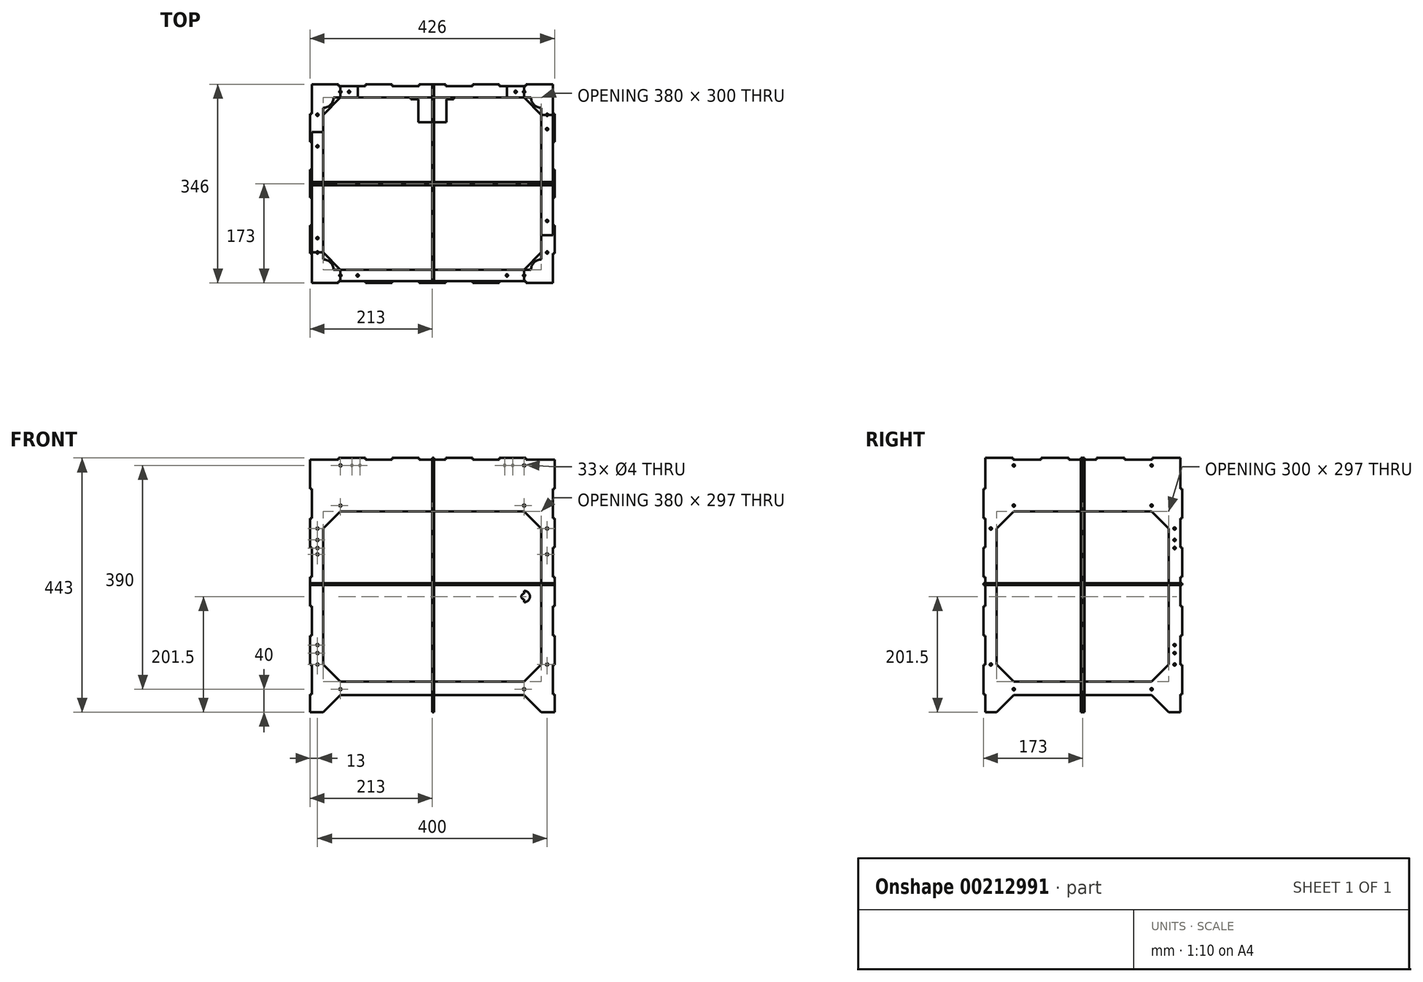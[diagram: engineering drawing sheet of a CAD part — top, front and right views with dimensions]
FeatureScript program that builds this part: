
annotation { "Feature Type Name" : "Feature", "Feature Type Description" : "" }
export const myFeature = defineFeature(function(context is Context, id is Id, definition is map)
    precondition{}
    {
        {
            assignVariable(context, id + "F0", {"name" : "thick", "anyValue" : 3});
        }
        {
            var Q0;
            Q0=qCreatedBy(makeId("Top.planeOp"),FACE);
            var sketch = newSketch(context, id + "F1", { "sketchPlane" : qUnion([Q0])});
            skLineSegment(sketch, "E0.bottom", {"start": v(213, -173) * mm, "end": v(-213, -173) * mm});
            skLineSegment(sketch, "E0.top", {"start": v(213, 173) * mm, "end": v(-213, 173) * mm});
            skLineSegment(sketch, "E0.left", {"start": v(213, -173) * mm, "end": v(213, 173) * mm});
            skLineSegment(sketch, "E0.right", {"start": v(-213, -173) * mm, "end": v(-213, 173) * mm});
            skPoint(sketch, "E0.middle", {"position": v(0, 0) * mm});
            skLineSegment(sketch, "E1.bottom", {"start": v(160, -150) * mm, "end": v(-160, -150) * mm});
            skLineSegment(sketch, "E1.top", {"start": v(160, 150) * mm, "end": v(-160, 150) * mm});
            skLineSegment(sketch, "E1.left", {"start": v(190, -120) * mm, "end": v(190, 120) * mm});
            skLineSegment(sketch, "E1.right", {"start": v(-190, -120) * mm, "end": v(-190, 120) * mm});
            skLineSegment(sketch, "E2", {"start": v(-160, 150) * mm, "end": v(-190, 120) * mm});
            skLineSegment(sketch, "E3", {"start": v(-190, -120) * mm, "end": v(-160, -150) * mm});
            skLineSegment(sketch, "E4", {"start": v(190, -120) * mm, "end": v(160, -150) * mm});
            skLineSegment(sketch, "E5", {"start": v(190, 120) * mm, "end": v(160, 150) * mm});
            skPoint(sketch, "E6.orphan", {"position": v(-190, 150) * mm});
            skPoint(sketch, "E7.orphan", {"position": v(-190, -150) * mm});
            skPoint(sketch, "E8.orphan", {"position": v(190, -150) * mm});
            skPoint(sketch, "E9.orphan", {"position": v(190, 150) * mm});
            skCircle(sketch, "E10", {"center": v(-160, 160) * mm, "radius": 2 * mm});
            skCircle(sketch, "E11", {"center": v(160, 160) * mm, "radius": 2 * mm});
            skCircle(sketch, "E12", {"center": v(-200, 120) * mm, "radius": 2 * mm});
            skCircle(sketch, "E13", {"center": v(-200, -120) * mm, "radius": 2 * mm});
            skCircle(sketch, "E14", {"center": v(-160, -160) * mm, "radius": 2 * mm});
            skCircle(sketch, "E15", {"center": v(160, -160) * mm, "radius": 2 * mm});
            skCircle(sketch, "E16", {"center": v(200, -120) * mm, "radius": 2 * mm});
            skCircle(sketch, "E17", {"center": v(200, 120) * mm, "radius": 2 * mm});
            skLineSegment(sketch, "E18", {"start": v(-163.33, -173) * mm, "end": v(-163.33, -170) * mm});
            skLineSegment(sketch, "E19", {"start": v(-163.33, -170) * mm, "end": v(-116.67, -170) * mm});
            skLineSegment(sketch, "E20", {"start": v(-116.67, -170) * mm, "end": v(-116.67, -173) * mm});
            skLineSegment(sketch, "E21.1.0.0", {"start": v(-70, -173) * mm, "end": v(-70, -170) * mm});
            skLineSegment(sketch, "E21.1.0.1", {"start": v(-70, -170) * mm, "end": v(-23.33, -170) * mm});
            skLineSegment(sketch, "E21.1.0.2", {"start": v(-23.33, -170) * mm, "end": v(-23.33, -173) * mm});
            skLineSegment(sketch, "E21.2.0.0", {"start": v(23.33, -173) * mm, "end": v(23.33, -170) * mm});
            skLineSegment(sketch, "E21.2.0.1", {"start": v(23.33, -170) * mm, "end": v(70, -170) * mm});
            skLineSegment(sketch, "E21.2.0.2", {"start": v(70, -170) * mm, "end": v(70, -173) * mm});
            skLineSegment(sketch, "E21.3.0.0", {"start": v(116.67, -173) * mm, "end": v(116.67, -170) * mm});
            skLineSegment(sketch, "E21.3.0.1", {"start": v(116.67, -170) * mm, "end": v(163.33, -170) * mm});
            skLineSegment(sketch, "E21.3.0.2", {"start": v(163.33, -170) * mm, "end": v(163.33, -173) * mm});
            skLineSegment(sketch, "E21.direction1", {"start": v(-163.33, -173) * mm, "end": v(-70, -173) * mm, "construction": true});
            skLineSegment(sketch, "E22", {"start": v(-163.33, 173) * mm, "end": v(-163.33, 170) * mm});
            skLineSegment(sketch, "E23", {"start": v(-163.33, 170) * mm, "end": v(-116.67, 170) * mm});
            skLineSegment(sketch, "E24", {"start": v(-116.67, 170) * mm, "end": v(-116.67, 173) * mm});
            skLineSegment(sketch, "E25.1.0.0", {"start": v(-70, 173) * mm, "end": v(-70, 170) * mm});
            skLineSegment(sketch, "E25.1.0.1", {"start": v(-70, 170) * mm, "end": v(-23.33, 170) * mm});
            skLineSegment(sketch, "E25.1.0.2", {"start": v(-23.33, 170) * mm, "end": v(-23.33, 173) * mm});
            skLineSegment(sketch, "E25.2.0.0", {"start": v(23.33, 173) * mm, "end": v(23.33, 170) * mm});
            skLineSegment(sketch, "E25.2.0.1", {"start": v(23.33, 170) * mm, "end": v(70, 170) * mm});
            skLineSegment(sketch, "E25.2.0.2", {"start": v(70, 170) * mm, "end": v(70, 173) * mm});
            skLineSegment(sketch, "E25.3.0.0", {"start": v(116.67, 173) * mm, "end": v(116.67, 170) * mm});
            skLineSegment(sketch, "E25.3.0.1", {"start": v(116.67, 170) * mm, "end": v(163.33, 170) * mm});
            skLineSegment(sketch, "E25.3.0.2", {"start": v(163.33, 170) * mm, "end": v(163.33, 173) * mm});
            skLineSegment(sketch, "E25.direction1", {"start": v(-163.33, 170) * mm, "end": v(-70, 170) * mm, "construction": true});
            skLineSegment(sketch, "E26", {"start": v(-213, -121.43) * mm, "end": v(-210, -121.43) * mm});
            skLineSegment(sketch, "E27", {"start": v(-210, -121.43) * mm, "end": v(-210, -170) * mm});
            skLineSegment(sketch, "E28", {"start": v(-210, -170) * mm, "end": v(-213, -170) * mm});
            skLineSegment(sketch, "E29.0.1.0", {"start": v(-213, -24.29) * mm, "end": v(-210, -24.29) * mm});
            skLineSegment(sketch, "E29.0.1.1", {"start": v(-210, -24.29) * mm, "end": v(-210, -72.86) * mm});
            skLineSegment(sketch, "E29.0.1.2", {"start": v(-210, -72.86) * mm, "end": v(-213, -72.86) * mm});
            skLineSegment(sketch, "E29.0.2.0", {"start": v(-213, 72.86) * mm, "end": v(-210, 72.86) * mm});
            skLineSegment(sketch, "E29.0.2.1", {"start": v(-210, 72.86) * mm, "end": v(-210, 24.29) * mm});
            skLineSegment(sketch, "E29.0.2.2", {"start": v(-210, 24.29) * mm, "end": v(-213, 24.29) * mm});
            skLineSegment(sketch, "E29.0.3.0", {"start": v(-213, 170) * mm, "end": v(-210, 170) * mm});
            skLineSegment(sketch, "E29.0.3.1", {"start": v(-210, 170) * mm, "end": v(-210, 121.43) * mm});
            skLineSegment(sketch, "E29.0.3.2", {"start": v(-210, 121.43) * mm, "end": v(-213, 121.43) * mm});
            skLineSegment(sketch, "E29.direction1", {"start": v(-213, -121.43) * mm, "end": v(-188, -121.43) * mm, "construction": true});
            skLineSegment(sketch, "E29.direction2", {"start": v(-213, -121.43) * mm, "end": v(-213, -24.29) * mm, "construction": true});
            skLineSegment(sketch, "E30", {"start": v(-210, -173) * mm, "end": v(-210, -170) * mm});
            skLineSegment(sketch, "E31", {"start": v(-210, 173) * mm, "end": v(-210, 170) * mm});
            skLineSegment(sketch, "E32", {"start": v(210, -173) * mm, "end": v(210, -170) * mm});
            skLineSegment(sketch, "E33", {"start": v(210, 173) * mm, "end": v(210, 170) * mm});
            skLineSegment(sketch, "E34", {"start": v(213, -170) * mm, "end": v(210, -170) * mm});
            skLineSegment(sketch, "E35", {"start": v(210, -170) * mm, "end": v(210, -121.43) * mm});
            skLineSegment(sketch, "E36", {"start": v(210, -121.43) * mm, "end": v(213, -121.43) * mm});
            skLineSegment(sketch, "E37.0.1.0", {"start": v(210, -24.29) * mm, "end": v(213, -24.29) * mm});
            skLineSegment(sketch, "E37.0.1.1", {"start": v(210, -72.86) * mm, "end": v(210, -24.29) * mm});
            skLineSegment(sketch, "E37.0.1.2", {"start": v(213, -72.86) * mm, "end": v(210, -72.86) * mm});
            skLineSegment(sketch, "E37.0.2.0", {"start": v(210, 72.86) * mm, "end": v(213, 72.86) * mm});
            skLineSegment(sketch, "E37.0.2.1", {"start": v(210, 24.29) * mm, "end": v(210, 72.86) * mm});
            skLineSegment(sketch, "E37.0.2.2", {"start": v(213, 24.29) * mm, "end": v(210, 24.29) * mm});
            skLineSegment(sketch, "E37.0.3.0", {"start": v(210, 170) * mm, "end": v(213, 170) * mm});
            skLineSegment(sketch, "E37.0.3.1", {"start": v(210, 121.43) * mm, "end": v(210, 170) * mm});
            skLineSegment(sketch, "E37.0.3.2", {"start": v(213, 121.43) * mm, "end": v(210, 121.43) * mm});
            skLineSegment(sketch, "E37.direction1", {"start": v(210, -121.43) * mm, "end": v(235, -121.43) * mm, "construction": true});
            skLineSegment(sketch, "E37.direction2", {"start": v(210, -121.43) * mm, "end": v(210, -24.29) * mm, "construction": true});
            skCircle(sketch, "E38", {"center": v(-140, 160) * mm, "radius": 2 * mm, "construction": true});
            skCircle(sketch, "E39", {"center": v(-126, 160) * mm, "radius": 2 * mm, "construction": true});
            skCircle(sketch, "E40", {"center": v(140, 160) * mm, "radius": 2 * mm, "construction": true});
            skCircle(sketch, "E41", {"center": v(126, 160) * mm, "radius": 2 * mm, "construction": true});
            skPoint(sketch, "E42.centerSnap0", {"position": v(-210, 48.57) * mm});
            skSolve(sketch);
        }
        {
            var Q0;
            Q0=makeQuery(id+"F1.imprint","IMPRINT",FACE,{"disambiguationData":[TD([[makeQuery(id+"F1.imprint","IMPRINT",EDGE,{"derivedFrom":sQuery(id+"F1.wireOp",EDGE,"E0.bottom")}),-1.0]])]});
            extrude(context, id + "F2", {"entities" : qUnion([Q0]), "depth" : (getVariable(context, 'thick')) * mm});
        }
        {
            var Q0;
            Q0=qCreatedBy(makeId("Front.planeOp"),FACE);
            var sketch = newSketch(context, id + "F3", { "sketchPlane" : qUnion([Q0])});
            skLineSegment(sketch, "E43.bottom", {"start": v(213, -221.5) * mm, "end": v(190, -221.5) * mm});
            skLineSegment(sketch, "E43.top", {"start": v(213, 221.5) * mm, "end": v(-213, 221.5) * mm});
            skLineSegment(sketch, "E43.left", {"start": v(213, -221.5) * mm, "end": v(213, 221.5) * mm});
            skLineSegment(sketch, "E43.right", {"start": v(-213, -221.5) * mm, "end": v(-213, 221.5) * mm});
            skPoint(sketch, "E43.middle", {"position": v(0, 0) * mm});
            skLineSegment(sketch, "E44.bottom", {"start": v(160, 128.5) * mm, "end": v(-160, 128.5) * mm});
            skLineSegment(sketch, "E44.top", {"start": v(160, -168.5) * mm, "end": v(-160, -168.5) * mm});
            skLineSegment(sketch, "E44.left", {"start": v(190, 98.5) * mm, "end": v(190, -138.5) * mm});
            skLineSegment(sketch, "E44.right", {"start": v(-190, 98.5) * mm, "end": v(-190, -138.5) * mm});
            skPoint(sketch, "E44.middle", {"position": v(0, -20) * mm});
            skLineSegment(sketch, "E45", {"start": v(-160, 128.5) * mm, "end": v(-190, 98.5) * mm});
            skLineSegment(sketch, "E46", {"start": v(-190, -138.5) * mm, "end": v(-160, -168.5) * mm});
            skLineSegment(sketch, "E47", {"start": v(190, -138.5) * mm, "end": v(160, -168.5) * mm});
            skLineSegment(sketch, "E48", {"start": v(160, 128.5) * mm, "end": v(190, 98.5) * mm});
            skPoint(sketch, "E49.orphan", {"position": v(-190, 128.5) * mm});
            skPoint(sketch, "E50.orphan", {"position": v(-190, -168.5) * mm});
            skPoint(sketch, "E51.orphan", {"position": v(190, 128.5) * mm});
            skPoint(sketch, "E52.orphan", {"position": v(190, -168.5) * mm});
            skLineSegment(sketch, "E53", {"start": v(-190, -221.5) * mm, "end": v(-160, -191.5) * mm});
            skLineSegment(sketch, "E54", {"start": v(-160, -191.5) * mm, "end": v(160, -191.5) * mm});
            skLineSegment(sketch, "E55", {"start": v(160, -191.5) * mm, "end": v(190, -221.5) * mm});
            skLineSegment(sketch, "E56.trimOffspring", {"start": v(-190, -221.5) * mm, "end": v(-213, -221.5) * mm});
            skCircle(sketch, "E57", {"center": v(-160, 208.5) * mm, "radius": 2 * mm});
            skCircle(sketch, "E58", {"center": v(160, 208.5) * mm, "radius": 2 * mm});
            skCircle(sketch, "E59", {"center": v(-160, 138.5) * mm, "radius": 2 * mm});
            skCircle(sketch, "E60", {"center": v(160, 138.5) * mm, "radius": 2 * mm});
            skCircle(sketch, "E61", {"center": v(200, 98.5) * mm, "radius": 2 * mm});
            skCircle(sketch, "E62", {"center": v(-200, 98.5) * mm, "radius": 2 * mm});
            skCircle(sketch, "E63", {"center": v(200, -138.5) * mm, "radius": 2 * mm});
            skCircle(sketch, "E64", {"center": v(160, -181.5) * mm, "radius": 2 * mm});
            skCircle(sketch, "E65", {"center": v(-160, -181.5) * mm, "radius": 2 * mm});
            skCircle(sketch, "E66", {"center": v(-200, -138.5) * mm, "radius": 2 * mm});
            skCircle(sketch, "E67", {"center": v(-200, 78.5) * mm, "radius": 2 * mm});
            skCircle(sketch, "E68", {"center": v(-200, 64.5) * mm, "radius": 2 * mm});
            skCircle(sketch, "E69", {"center": v(-200, -118.5) * mm, "radius": 2 * mm});
            skCircle(sketch, "E70", {"center": v(-200, -104.5) * mm, "radius": 2 * mm});
            skLineSegment(sketch, "E71", {"start": v(-210, 221.5) * mm, "end": v(-210, 218.5) * mm});
            skLineSegment(sketch, "E72", {"start": v(-210, 218.5) * mm, "end": v(-163.33, 218.5) * mm});
            skLineSegment(sketch, "E73", {"start": v(-163.33, 218.5) * mm, "end": v(-163.33, 221.5) * mm});
            skLineSegment(sketch, "E74.1.0.0", {"start": v(-116.67, 221.5) * mm, "end": v(-116.67, 218.5) * mm});
            skLineSegment(sketch, "E74.1.0.1", {"start": v(-116.67, 218.5) * mm, "end": v(-70, 218.5) * mm});
            skLineSegment(sketch, "E74.1.0.2", {"start": v(-70, 218.5) * mm, "end": v(-70, 221.5) * mm});
            skLineSegment(sketch, "E74.2.0.0", {"start": v(-23.33, 221.5) * mm, "end": v(-23.33, 218.5) * mm});
            skLineSegment(sketch, "E74.2.0.1", {"start": v(-23.33, 218.5) * mm, "end": v(23.33, 218.5) * mm});
            skLineSegment(sketch, "E74.2.0.2", {"start": v(23.33, 218.5) * mm, "end": v(23.33, 221.5) * mm});
            skLineSegment(sketch, "E74.3.0.0", {"start": v(70, 221.5) * mm, "end": v(70, 218.5) * mm});
            skLineSegment(sketch, "E74.3.0.1", {"start": v(70, 218.5) * mm, "end": v(116.67, 218.5) * mm});
            skLineSegment(sketch, "E74.3.0.2", {"start": v(116.67, 218.5) * mm, "end": v(116.67, 221.5) * mm});
            skLineSegment(sketch, "E74.4.0.0", {"start": v(163.33, 221.5) * mm, "end": v(163.33, 218.5) * mm});
            skLineSegment(sketch, "E74.4.0.1", {"start": v(163.33, 218.5) * mm, "end": v(210, 218.5) * mm});
            skLineSegment(sketch, "E74.4.0.2", {"start": v(210, 218.5) * mm, "end": v(210, 221.5) * mm});
            skLineSegment(sketch, "E74.direction1", {"start": v(-210, 218.5) * mm, "end": v(-116.67, 218.5) * mm, "construction": true});
            skLineSegment(sketch, "E75", {"start": v(-213, 218.5) * mm, "end": v(-210, 218.5) * mm});
            skLineSegment(sketch, "E76", {"start": v(213, 218.5) * mm, "end": v(210, 218.5) * mm});
            skLineSegment(sketch, "E77", {"start": v(-213, -139.28) * mm, "end": v(-210, -139.28) * mm});
            skLineSegment(sketch, "E78", {"start": v(-210, -139.28) * mm, "end": v(-210, -190.39) * mm});
            skLineSegment(sketch, "E79", {"start": v(-210, -190.39) * mm, "end": v(-213, -190.39) * mm});
            skLineSegment(sketch, "E80.0.1.0", {"start": v(-210, -37.06) * mm, "end": v(-210, -88.17) * mm});
            skLineSegment(sketch, "E80.0.1.1", {"start": v(-213, -37.06) * mm, "end": v(-210, -37.06) * mm});
            skLineSegment(sketch, "E80.0.1.2", {"start": v(-210, -88.17) * mm, "end": v(-213, -88.17) * mm});
            skLineSegment(sketch, "E80.0.2.0", {"start": v(-210, 65.17) * mm, "end": v(-210, 14.06) * mm});
            skLineSegment(sketch, "E80.0.2.1", {"start": v(-213, 65.17) * mm, "end": v(-210, 65.17) * mm});
            skLineSegment(sketch, "E80.0.2.2", {"start": v(-210, 14.06) * mm, "end": v(-213, 14.06) * mm});
            skLineSegment(sketch, "E80.0.3.0", {"start": v(-210, 167.39) * mm, "end": v(-210, 116.28) * mm});
            skLineSegment(sketch, "E80.0.3.1", {"start": v(-213, 167.39) * mm, "end": v(-210, 167.39) * mm});
            skLineSegment(sketch, "E80.0.3.2", {"start": v(-210, 116.28) * mm, "end": v(-213, 116.28) * mm});
            skLineSegment(sketch, "E80.direction1", {"start": v(-210, -190.39) * mm, "end": v(-185.37, -190.39) * mm, "construction": true});
            skLineSegment(sketch, "E80.direction2", {"start": v(-210, -190.39) * mm, "end": v(-210, -88.17) * mm, "construction": true});
            skLineSegment(sketch, "E81", {"start": v(213, -190.39) * mm, "end": v(210, -190.39) * mm});
            skLineSegment(sketch, "E82", {"start": v(210, -190.39) * mm, "end": v(210, -139.28) * mm});
            skLineSegment(sketch, "E83", {"start": v(210, -139.28) * mm, "end": v(213, -139.28) * mm});
            skLineSegment(sketch, "E84.0.1.0", {"start": v(210, -37.06) * mm, "end": v(213, -37.06) * mm});
            skLineSegment(sketch, "E84.0.1.1", {"start": v(210, -88.17) * mm, "end": v(210, -37.06) * mm});
            skLineSegment(sketch, "E84.0.1.2", {"start": v(213, -88.17) * mm, "end": v(210, -88.17) * mm});
            skLineSegment(sketch, "E84.0.2.0", {"start": v(210, 65.17) * mm, "end": v(213, 65.17) * mm});
            skLineSegment(sketch, "E84.0.2.1", {"start": v(210, 14.06) * mm, "end": v(210, 65.17) * mm});
            skLineSegment(sketch, "E84.0.2.2", {"start": v(213, 14.06) * mm, "end": v(210, 14.06) * mm});
            skLineSegment(sketch, "E84.0.3.0", {"start": v(210, 167.39) * mm, "end": v(213, 167.39) * mm});
            skLineSegment(sketch, "E84.0.3.1", {"start": v(210, 116.28) * mm, "end": v(210, 167.39) * mm});
            skLineSegment(sketch, "E84.0.3.2", {"start": v(213, 116.28) * mm, "end": v(210, 116.28) * mm});
            skLineSegment(sketch, "E84.direction1", {"start": v(210, -139.28) * mm, "end": v(235, -139.28) * mm, "construction": true});
            skLineSegment(sketch, "E84.direction2", {"start": v(210, -139.28) * mm, "end": v(210, -37.06) * mm, "construction": true});
            skCircle(sketch, "E85", {"center": v(140, 208.5) * mm, "radius": 2 * mm});
            skCircle(sketch, "E86", {"center": v(126, 208.5) * mm, "radius": 2 * mm});
            skCircle(sketch, "E87", {"center": v(-140, 208.5) * mm, "radius": 2 * mm});
            skCircle(sketch, "E88", {"center": v(-126, 208.5) * mm, "radius": 2 * mm});
            skCircle(sketch, "E89", {"center": v(200, 53.5) * mm, "radius": 2 * mm});
            skArc(sketch, "E90", {"start": v(160, -10) * mm, "mid": v(170, -20) * mm, "end": v(160, -30) * mm});
            skArc(sketch, "E91", {"start": v(160, -15) * mm, "mid": v(155, -20) * mm, "end": v(160, -25) * mm});
            skLineSegment(sketch, "E92", {"start": v(160, -15) * mm, "end": v(160, -10) * mm});
            skLineSegment(sketch, "E93", {"start": v(160, -25) * mm, "end": v(160, -30) * mm});
            skCircle(sketch, "E94", {"center": v(-200, 53.5) * mm, "radius": 2 * mm});
            skSolve(sketch);
        }
        {
            var Q0;
            Q0=makeQuery(id+"F3.imprint","IMPRINT",FACE,{"disambiguationData":[TD([[makeQuery(id+"F3.imprint","IMPRINT",EDGE,{"derivedFrom":sQuery(id+"F3.wireOp",EDGE,"E43.bottom")}),-1.0]])]});
            var Q1;
            Q1=makeQuery(id+"F3.imprint","IMPRINT",FACE,{"disambiguationData":[TD([[makeQuery(id+"F3.imprint","IMPRINT",EDGE,{"derivedFrom":sQuery(id+"F3.wireOp",EDGE,"E87")}),1.0]])]});
            var Q2;
            Q2=makeQuery(id+"F3.imprint","IMPRINT",FACE,{"disambiguationData":[TD([[makeQuery(id+"F3.imprint","IMPRINT",EDGE,{"derivedFrom":sQuery(id+"F3.wireOp",EDGE,"E88")}),1.0]])]});
            var Q3;
            Q3=makeQuery(id+"F3.imprint","IMPRINT",FACE,{"disambiguationData":[TD([[makeQuery(id+"F3.imprint","IMPRINT",EDGE,{"derivedFrom":sQuery(id+"F3.wireOp",EDGE,"E86")}),1.0]])]});
            var Q4;
            Q4=makeQuery(id+"F3.imprint","IMPRINT",FACE,{"disambiguationData":[TD([[makeQuery(id+"F3.imprint","IMPRINT",EDGE,{"derivedFrom":sQuery(id+"F3.wireOp",EDGE,"E85")}),1.0]])]});
            extrude(context, id + "F4", {"entities" : qUnion([Q0, Q1, Q2, Q3, Q4]), "depth" : (getVariable(context, 'thick')) * mm});
        }
        {
            var Q0;
            Q0=makeQuery(id+"F3.imprint","IMPRINT",FACE,{"disambiguationData":[TD([[makeQuery(id+"F3.imprint","IMPRINT",EDGE,{"derivedFrom":sQuery(id+"F3.wireOp",EDGE,"E43.bottom")}),-1.0]])]});
            var Q1;
            Q1=makeQuery(id+"F3.imprint","IMPRINT",FACE,{"disambiguationData":[TD([[makeQuery(id+"F3.imprint","IMPRINT",EDGE,{"derivedFrom":sQuery(id+"F3.wireOp",EDGE,"E44.bottom")}),1.0]])]});
            var Q2;
            Q2=makeQuery(id+"F3.imprint","IMPRINT",FACE,{"disambiguationData":[TD([[makeQuery(id+"F3.imprint","IMPRINT",EDGE,{"derivedFrom":sQuery(id+"F3.wireOp",EDGE,"E67")}),1.0]])]});
            var Q3;
            Q3=makeQuery(id+"F3.imprint","IMPRINT",FACE,{"disambiguationData":[TD([[makeQuery(id+"F3.imprint","IMPRINT",EDGE,{"derivedFrom":sQuery(id+"F3.wireOp",EDGE,"E70")}),1.0]])]});
            var Q4;
            Q4=makeQuery(id+"F3.imprint","IMPRINT",FACE,{"disambiguationData":[TD([[makeQuery(id+"F3.imprint","IMPRINT",EDGE,{"derivedFrom":sQuery(id+"F3.wireOp",EDGE,"E69")}),1.0]])]});
            var Q5;
            Q5=makeQuery(id+"F3.imprint","IMPRINT",FACE,{"disambiguationData":[TD([[makeQuery(id+"F3.imprint","IMPRINT",EDGE,{"derivedFrom":sQuery(id+"F3.wireOp",EDGE,"E90")}),-1.0]])]});
            extrude(context, id + "F5", {"entities" : qUnion([Q0, Q1, Q2, Q3, Q4, Q5]), "oppositeDirection" : true, "depth" : (getVariable(context, 'thick')) * mm});
        }
        {
            var Q0;
            Q0=qCreatedBy(makeId("Right.planeOp"),FACE);
            var sketch = newSketch(context, id + "F6", { "sketchPlane" : qUnion([Q0])});
            skLineSegment(sketch, "E95.bottom", {"start": v(-173, -221.5) * mm, "end": v(173, -221.5) * mm});
            skLineSegment(sketch, "E95.top", {"start": v(-173, 221.5) * mm, "end": v(173, 221.5) * mm});
            skLineSegment(sketch, "E95.left", {"start": v(-173, -221.5) * mm, "end": v(-173, 221.5) * mm});
            skLineSegment(sketch, "E95.right", {"start": v(173, -221.5) * mm, "end": v(173, 221.5) * mm});
            skPoint(sketch, "E95.middle", {"position": v(0, 0) * mm});
            skLineSegment(sketch, "E96.bottom", {"start": v(-120, 128.5) * mm, "end": v(120, 128.5) * mm});
            skLineSegment(sketch, "E96.top", {"start": v(-120, -168.5) * mm, "end": v(120, -168.5) * mm});
            skLineSegment(sketch, "E96.left", {"start": v(-150, 98.5) * mm, "end": v(-150, -138.5) * mm});
            skLineSegment(sketch, "E96.right", {"start": v(150, 98.5) * mm, "end": v(150, -138.5) * mm});
            skPoint(sketch, "E96.middle", {"position": v(0, -20) * mm});
            skLineSegment(sketch, "E97", {"start": v(120, 128.5) * mm, "end": v(150, 98.5) * mm});
            skLineSegment(sketch, "E98", {"start": v(-120, 128.5) * mm, "end": v(-150, 98.5) * mm});
            skLineSegment(sketch, "E99", {"start": v(-150, -138.5) * mm, "end": v(-120, -168.5) * mm});
            skLineSegment(sketch, "E100", {"start": v(120, -168.5) * mm, "end": v(150, -138.5) * mm});
            skPoint(sketch, "E101.orphan", {"position": v(150, 128.5) * mm});
            skPoint(sketch, "E102.orphan", {"position": v(-150, 128.5) * mm});
            skPoint(sketch, "E103.orphan", {"position": v(-150, -168.5) * mm});
            skPoint(sketch, "E104.orphan", {"position": v(150, -168.5) * mm});
            skLineSegment(sketch, "E105", {"start": v(150, -221.5) * mm, "end": v(120, -191.5) * mm});
            skLineSegment(sketch, "E106", {"start": v(120, -191.5) * mm, "end": v(-120, -191.5) * mm});
            skLineSegment(sketch, "E107", {"start": v(-120, -191.5) * mm, "end": v(-150, -221.5) * mm});
            skCircle(sketch, "E108", {"center": v(120, 138.5) * mm, "radius": 2 * mm});
            skCircle(sketch, "E109", {"center": v(-120, 138.5) * mm, "radius": 2 * mm});
            skCircle(sketch, "E110", {"center": v(-120, 208.5) * mm, "radius": 2 * mm});
            skCircle(sketch, "E111", {"center": v(120, 208.5) * mm, "radius": 2 * mm});
            skCircle(sketch, "E112", {"center": v(160, 98.5) * mm, "radius": 2 * mm});
            skCircle(sketch, "E113", {"center": v(160, -138.5) * mm, "radius": 2 * mm});
            skCircle(sketch, "E114", {"center": v(-160, 98.5) * mm, "radius": 2 * mm});
            skCircle(sketch, "E115", {"center": v(-160, -138.5) * mm, "radius": 2 * mm});
            skCircle(sketch, "E116", {"center": v(120, -181.5) * mm, "radius": 2 * mm});
            skCircle(sketch, "E117", {"center": v(-120, -181.5) * mm, "radius": 2 * mm});
            skCircle(sketch, "E118", {"center": v(160, 78.5) * mm, "radius": 2 * mm});
            skCircle(sketch, "E119", {"center": v(160, 64.5) * mm, "radius": 2 * mm});
            skCircle(sketch, "E120", {"center": v(160, -118.5) * mm, "radius": 2 * mm});
            skCircle(sketch, "E121", {"center": v(160, -104.5) * mm, "radius": 2 * mm});
            skLineSegment(sketch, "E122", {"start": v(-170, 221.5) * mm, "end": v(-170, 218.5) * mm});
            skLineSegment(sketch, "E123", {"start": v(170, 221.5) * mm, "end": v(170, 218.5) * mm});
            skLineSegment(sketch, "E124", {"start": v(173, -241.5) * mm, "end": v(170, -241.5) * mm});
            skLineSegment(sketch, "E125", {"start": v(170, -241.5) * mm, "end": v(170, -190.39) * mm});
            skLineSegment(sketch, "E126", {"start": v(170, -190.39) * mm, "end": v(173, -190.39) * mm});
            skLineSegment(sketch, "E127", {"start": v(-173, -241.5) * mm, "end": v(-170, -241.5) * mm});
            skLineSegment(sketch, "E128", {"start": v(-170, -241.5) * mm, "end": v(-170, -190.39) * mm});
            skLineSegment(sketch, "E129", {"start": v(-170, -190.39) * mm, "end": v(-173, -190.39) * mm});
            skLineSegment(sketch, "E130.0.1.0", {"start": v(173, -139.28) * mm, "end": v(170, -139.28) * mm});
            skLineSegment(sketch, "E130.0.1.1", {"start": v(170, -139.28) * mm, "end": v(170, -88.17) * mm});
            skLineSegment(sketch, "E130.0.1.2", {"start": v(170, -88.17) * mm, "end": v(173, -88.17) * mm});
            skLineSegment(sketch, "E130.0.1.3", {"start": v(-170, -88.17) * mm, "end": v(-173, -88.17) * mm});
            skLineSegment(sketch, "E130.0.1.4", {"start": v(-170, -139.28) * mm, "end": v(-170, -88.17) * mm});
            skLineSegment(sketch, "E130.0.1.5", {"start": v(-173, -139.28) * mm, "end": v(-170, -139.28) * mm});
            skLineSegment(sketch, "E130.0.2.0", {"start": v(173, -37.06) * mm, "end": v(170, -37.06) * mm});
            skLineSegment(sketch, "E130.0.2.1", {"start": v(170, -37.06) * mm, "end": v(170, 14.06) * mm});
            skLineSegment(sketch, "E130.0.2.2", {"start": v(170, 14.06) * mm, "end": v(173, 14.06) * mm});
            skLineSegment(sketch, "E130.0.2.3", {"start": v(-170, 14.06) * mm, "end": v(-173, 14.06) * mm});
            skLineSegment(sketch, "E130.0.2.4", {"start": v(-170, -37.06) * mm, "end": v(-170, 14.06) * mm});
            skLineSegment(sketch, "E130.0.2.5", {"start": v(-173, -37.06) * mm, "end": v(-170, -37.06) * mm});
            skLineSegment(sketch, "E130.0.3.0", {"start": v(173, 65.17) * mm, "end": v(170, 65.17) * mm});
            skLineSegment(sketch, "E130.0.3.1", {"start": v(170, 65.17) * mm, "end": v(170, 116.28) * mm});
            skLineSegment(sketch, "E130.0.3.2", {"start": v(170, 116.28) * mm, "end": v(173, 116.28) * mm});
            skLineSegment(sketch, "E130.0.3.3", {"start": v(-170, 116.28) * mm, "end": v(-173, 116.28) * mm});
            skLineSegment(sketch, "E130.0.3.4", {"start": v(-170, 65.17) * mm, "end": v(-170, 116.28) * mm});
            skLineSegment(sketch, "E130.0.3.5", {"start": v(-173, 65.17) * mm, "end": v(-170, 65.17) * mm});
            skLineSegment(sketch, "E130.0.4.0", {"start": v(173, 167.39) * mm, "end": v(170, 167.39) * mm});
            skLineSegment(sketch, "E130.0.4.1", {"start": v(170, 167.39) * mm, "end": v(170, 218.5) * mm});
            skLineSegment(sketch, "E130.0.4.2", {"start": v(170, 218.5) * mm, "end": v(173, 218.5) * mm});
            skLineSegment(sketch, "E130.0.4.3", {"start": v(-170, 218.5) * mm, "end": v(-173, 218.5) * mm});
            skLineSegment(sketch, "E130.0.4.4", {"start": v(-170, 167.39) * mm, "end": v(-170, 218.5) * mm});
            skLineSegment(sketch, "E130.0.4.5", {"start": v(-173, 167.39) * mm, "end": v(-170, 167.39) * mm});
            skLineSegment(sketch, "E130.direction1", {"start": v(170, -241.5) * mm, "end": v(186.73, -241.5) * mm, "construction": true});
            skLineSegment(sketch, "E130.direction2", {"start": v(170, -241.5) * mm, "end": v(170, -139.28) * mm, "construction": true});
            skLineSegment(sketch, "E131", {"start": v(-72.86, 221.5) * mm, "end": v(-72.86, 218.5) * mm});
            skLineSegment(sketch, "E132", {"start": v(-72.86, 218.5) * mm, "end": v(-121.43, 218.5) * mm});
            skLineSegment(sketch, "E133", {"start": v(-121.43, 218.5) * mm, "end": v(-121.43, 221.5) * mm});
            skLineSegment(sketch, "E134.1.0.0", {"start": v(24.29, 221.5) * mm, "end": v(24.29, 218.5) * mm});
            skLineSegment(sketch, "E134.1.0.1", {"start": v(24.29, 218.5) * mm, "end": v(-24.29, 218.5) * mm});
            skLineSegment(sketch, "E134.1.0.2", {"start": v(-24.29, 218.5) * mm, "end": v(-24.29, 221.5) * mm});
            skLineSegment(sketch, "E134.2.0.0", {"start": v(121.43, 221.5) * mm, "end": v(121.43, 218.5) * mm});
            skLineSegment(sketch, "E134.2.0.1", {"start": v(121.43, 218.5) * mm, "end": v(72.86, 218.5) * mm});
            skLineSegment(sketch, "E134.2.0.2", {"start": v(72.86, 218.5) * mm, "end": v(72.86, 221.5) * mm});
            skLineSegment(sketch, "E134.direction1", {"start": v(-72.86, 218.5) * mm, "end": v(24.29, 218.5) * mm, "construction": true});
            skArc(sketch, "E135", {"start": v(-120, -10) * mm, "mid": v(-130, -20) * mm, "end": v(-120, -30) * mm});
            skArc(sketch, "E136", {"start": v(-120, -15) * mm, "mid": v(-115, -20) * mm, "end": v(-120, -25) * mm});
            skLineSegment(sketch, "E137", {"start": v(-120, -15) * mm, "end": v(-120, -10) * mm});
            skLineSegment(sketch, "E138", {"start": v(-120, -25) * mm, "end": v(-120, -30) * mm});
            skSolve(sketch);
        }
        {
            var Q0;
            Q0=makeQuery(id+"F6.imprint","IMPRINT",FACE,{"disambiguationData":[TD([[makeQuery(id+"F6.imprint","IMPRINT",EDGE,{"derivedFrom":sQuery(id+"F6.wireOp",EDGE,"E95.top")}),-1.0]])]});
            extrude(context, id + "F7", {"entities" : qUnion([Q0]), "depth" : (getVariable(context, 'thick')) * mm});
        }
        {
            var Q0;
            Q0=qCreatedBy(makeId("Top.planeOp"),FACE);
            var sketch = newSketch(context, id + "F8", { "sketchPlane" : qUnion([Q0])});
            skLineSegment(sketch, "E139.bottom", {"start": v(190, -150) * mm, "end": v(160, -150) * mm});
            skLineSegment(sketch, "E139.top", {"start": v(190, 150) * mm, "end": v(160, 150) * mm});
            skLineSegment(sketch, "E139.left", {"start": v(190, -150) * mm, "end": v(190, -90) * mm});
            skLineSegment(sketch, "E139.right", {"start": v(-190, -150) * mm, "end": v(-190, -120) * mm});
            skPoint(sketch, "E139.middle", {"position": v(0, 0) * mm});
            skLineSegment(sketch, "E140.bottom", {"start": v(-24.5, 150) * mm, "end": v(24.5, 150) * mm});
            skLineSegment(sketch, "E140.top", {"start": v(-24.5, 107) * mm, "end": v(24.5, 107) * mm});
            skLineSegment(sketch, "E140.left", {"start": v(-24.5, 147) * mm, "end": v(-24.5, 107) * mm});
            skLineSegment(sketch, "E140.right", {"start": v(24.5, 147) * mm, "end": v(24.5, 107) * mm});
            skLineSegment(sketch, "E141", {"start": v(0, 0) * mm, "end": v(0, 107) * mm, "construction": true});
            skLineSegment(sketch, "E142", {"start": v(-24.5, 147) * mm, "end": v(-37.5, 147) * mm});
            skLineSegment(sketch, "E143", {"start": v(-37.5, 147) * mm, "end": v(-37.5, 150) * mm});
            skLineSegment(sketch, "E144", {"start": v(24.5, 147) * mm, "end": v(37.5, 147) * mm});
            skLineSegment(sketch, "E145", {"start": v(37.5, 147) * mm, "end": v(37.5, 150) * mm});
            skLineSegment(sketch, "E146.bottom", {"start": v(-190, 90) * mm, "end": v(-210, 90) * mm});
            skLineSegment(sketch, "E146.top", {"start": v(-190, -120) * mm, "end": v(-210, -120) * mm});
            skLineSegment(sketch, "E146.right", {"start": v(-210, 90) * mm, "end": v(-210, -120) * mm});
            skLineSegment(sketch, "E147.bottom", {"start": v(190, 120) * mm, "end": v(210, 120) * mm});
            skLineSegment(sketch, "E147.top", {"start": v(190, -90) * mm, "end": v(210, -90) * mm});
            skLineSegment(sketch, "E147.right", {"start": v(210, 120) * mm, "end": v(210, -90) * mm});
            skLineSegment(sketch, "E148.top", {"start": v(-160, -170) * mm, "end": v(160, -170) * mm});
            skLineSegment(sketch, "E148.left", {"start": v(-160, -150) * mm, "end": v(-160, -170) * mm});
            skLineSegment(sketch, "E148.right", {"start": v(160, -150) * mm, "end": v(160, -170) * mm});
            skArc(sketch, "E149", {"start": v(190, -132) * mm, "mid": v(177.27, -137.27) * mm, "end": v(172, -150) * mm});
            skArc(sketch, "E150", {"start": v(-190, 132) * mm, "mid": v(-177.27, 137.27) * mm, "end": v(-172, 150) * mm});
            skArc(sketch, "E151", {"start": v(172, 150) * mm, "mid": v(177.27, 137.27) * mm, "end": v(190, 132) * mm});
            skCircle(sketch, "E152", {"center": v(200, 95) * mm, "radius": 2 * mm});
            skPoint(sketch, "E152.centerSnap0", {"position": v(200, 120) * mm});
            skCircle(sketch, "E153", {"center": v(200, -65) * mm, "radius": 2 * mm});
            skCircle(sketch, "E154", {"center": v(-200, -95) * mm, "radius": 2 * mm});
            skPoint(sketch, "E154.centerSnap0", {"position": v(-200, -120) * mm});
            skCircle(sketch, "E155", {"center": v(-200, 65) * mm, "radius": 2 * mm});
            skCircle(sketch, "E156", {"center": v(-130, -160) * mm, "radius": 2 * mm});
            skPoint(sketch, "E156.centerSnap0", {"position": v(-160, -160) * mm});
            skCircle(sketch, "E157", {"center": v(130, -160) * mm, "radius": 2 * mm});
            skLineSegment(sketch, "E158", {"start": v(-160, 150) * mm, "end": v(-160, 170) * mm});
            skLineSegment(sketch, "E159", {"start": v(-160, 170) * mm, "end": v(-130, 170) * mm});
            skLineSegment(sketch, "E160", {"start": v(-130, 170) * mm, "end": v(-130, 150) * mm});
            skLineSegment(sketch, "E161", {"start": v(160, 150) * mm, "end": v(160, 170) * mm});
            skLineSegment(sketch, "E162", {"start": v(160, 170) * mm, "end": v(130, 170) * mm});
            skLineSegment(sketch, "E163", {"start": v(130, 170) * mm, "end": v(130, 150) * mm});
            skCircle(sketch, "E164", {"center": v(-145, 160) * mm, "radius": 2 * mm});
            skPoint(sketch, "E164.centerSnap0", {"position": v(-130, 160) * mm});
            skPoint(sketch, "E164.centerSnap1", {"position": v(-145, 170) * mm});
            skCircle(sketch, "E165", {"center": v(145, 160) * mm, "radius": 2 * mm});
            skPoint(sketch, "E165.centerSnap0", {"position": v(145, 170) * mm});
            skPoint(sketch, "E165.centerSnap1", {"position": v(160, 160) * mm});
            skLineSegment(sketch, "E166.trimOffspring", {"start": v(130, 150) * mm, "end": v(-130, 150) * mm});
            skLineSegment(sketch, "E167.trimOffspring", {"start": v(-160, 150) * mm, "end": v(-190, 150) * mm});
            skLineSegment(sketch, "E168.trimOffspring", {"start": v(190, 120) * mm, "end": v(190, 150) * mm});
            skLineSegment(sketch, "E169.trimOffspring", {"start": v(-190, 90) * mm, "end": v(-190, 150) * mm});
            skLineSegment(sketch, "E170.trimOffspring", {"start": v(-160, -150) * mm, "end": v(-190, -150) * mm});
            skArc(sketch, "E171", {"start": v(-190, -132) * mm, "mid": v(-177.27, -137.27) * mm, "end": v(-172, -150) * mm});
            skSolve(sketch);
        }
        {
            var Q0;
            {var subQ11=sQuery(id+"F8.wireOp",EDGE,"E140.top");Q0=makeQuery(id+"F8.imprint","IMPRINT",FACE,{"disambiguationData":[TD([[makeQuery(id+"F8.imprint","IMPRINT",EDGE,{"derivedFrom":subQ11}),-1.0]])]});}
            var Q1;
            {var subQ0=sQuery(id+"F8.wireOp",EDGE,"E158");Q1=makeQuery(id+"F8.imprint","IMPRINT",FACE,{"disambiguationData":[TD([[makeQuery(id+"F8.imprint","IMPRINT",EDGE,{"derivedFrom":subQ0}),-1.0]])]});}
            var Q2;
            {var subQ1=sQuery(id+"F8.wireOp",EDGE,"E161");Q2=makeQuery(id+"F8.imprint","IMPRINT",FACE,{"disambiguationData":[TD([[makeQuery(id+"F8.imprint","IMPRINT",EDGE,{"derivedFrom":subQ1}),1.0]])]});}
            var Q3;
            Q3=makeQuery(id+"F8.imprint","IMPRINT",FACE,{"disambiguationData":[TD([[makeQuery(id+"F8.imprint","IMPRINT",EDGE,{"derivedFrom":sQuery(id+"F8.wireOp",EDGE,"E147.bottom")}),-1.0]])]});
            var Q4;
            Q4=makeQuery(id+"F8.imprint","IMPRINT",FACE,{"disambiguationData":[TD([[makeQuery(id+"F8.imprint","IMPRINT",EDGE,{"derivedFrom":sQuery(id+"F8.wireOp",EDGE,"E146.bottom")}),1.0]])]});
            var Q5;
            Q5=makeQuery(id+"F8.imprint","IMPRINT",FACE,{"disambiguationData":[TD([[makeQuery(id+"F8.imprint","IMPRINT",EDGE,{"derivedFrom":sQuery(id+"F8.wireOp",EDGE,"E148.bottom")}),-1.0]])]});
            extrude(context, id + "F9", {"entities" : qUnion([Q0, Q1, Q2, Q3, Q4, Q5]), "depth" : (getVariable(context, 'thick')) * mm});
        }
    });
